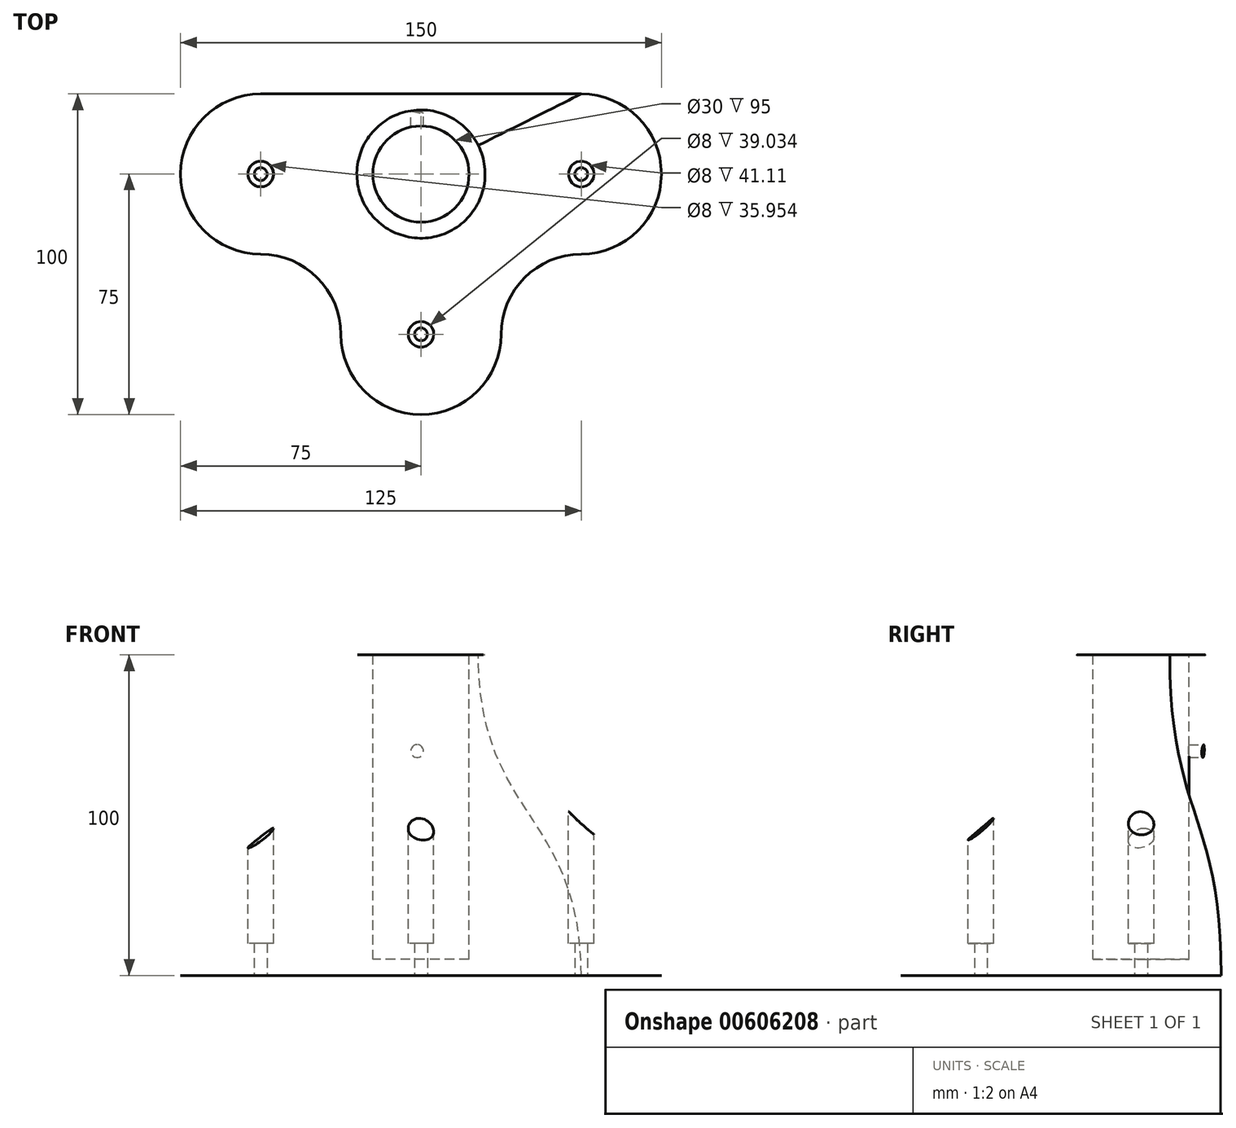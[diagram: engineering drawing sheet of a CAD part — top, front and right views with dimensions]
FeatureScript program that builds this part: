
annotation { "Feature Type Name" : "Feature", "Feature Type Description" : "" }
export const myFeature = defineFeature(function(context is Context, id is Id, definition is map)
    precondition{}
    {
        {
            var Q0;
            Q0=qCreatedBy(makeId("Top.planeOp"),FACE);
            var sketch = newSketch(context, id + "F0", { "sketchPlane" : qUnion([Q0])});
            skLineSegment(sketch, "E0.bottom", {"start": v(-25, 0) * mm, "end": v(-25, 0) * mm});
            skLineSegment(sketch, "E0.top", {"start": v(-25, 50) * mm, "end": v(-125, 50) * mm});
            skLineSegment(sketch, "E0.left", {"start": v(0, 25) * mm, "end": v(0, 25) * mm});
            skLineSegment(sketch, "E0.right", {"start": v(-150, 25) * mm, "end": v(-150, 25) * mm});
            skLineSegment(sketch, "E1", {"start": v(-100, -25) * mm, "end": v(-100, -25) * mm});
            skLineSegment(sketch, "E2", {"start": v(-75, -50) * mm, "end": v(-75, -50) * mm});
            skLineSegment(sketch, "E3", {"start": v(-50, -25) * mm, "end": v(-50, -25) * mm});
            skLineSegment(sketch, "E4.trimOffspring", {"start": v(-125, 0) * mm, "end": v(-125, 0) * mm});
            skPoint(sketch, "E5.visualSharp", {"position": v(0, 50) * mm});
            skArc(sketch, "E5.filletArc", {"start": v(0, 25) * mm, "mid": v(-7.32, 42.68) * mm, "end": v(-25, 50) * mm});
            skPoint(sketch, "E6.visualSharp", {"position": v(0, 0) * mm});
            skArc(sketch, "E6.filletArc", {"start": v(-25, 0) * mm, "mid": v(-7.32, 7.32) * mm, "end": v(0, 25) * mm});
            skPoint(sketch, "E7.visualSharp", {"position": v(-150, 50) * mm});
            skArc(sketch, "E7.filletArc", {"start": v(-125, 50) * mm, "mid": v(-142.68, 42.68) * mm, "end": v(-150, 25) * mm});
            skPoint(sketch, "E8.visualSharp", {"position": v(-150, 0) * mm});
            skArc(sketch, "E8.filletArc", {"start": v(-150, 25) * mm, "mid": v(-142.68, 7.32) * mm, "end": v(-125, 0) * mm});
            skPoint(sketch, "E9.visualSharp", {"position": v(-100, -50) * mm});
            skArc(sketch, "E9.filletArc", {"start": v(-100, -25) * mm, "mid": v(-92.68, -42.68) * mm, "end": v(-75, -50) * mm});
            skPoint(sketch, "E10.visualSharp", {"position": v(-50, -50) * mm});
            skArc(sketch, "E10.filletArc", {"start": v(-75, -50) * mm, "mid": v(-57.32, -42.68) * mm, "end": v(-50, -25) * mm});
            skPoint(sketch, "E11.visualSharp", {"position": v(-50, 0) * mm});
            skArc(sketch, "E11.filletArc", {"start": v(-25, 0) * mm, "mid": v(-42.68, -7.32) * mm, "end": v(-50, -25) * mm});
            skPoint(sketch, "E12.visualSharp", {"position": v(-100, 0) * mm});
            skArc(sketch, "E12.filletArc", {"start": v(-100, -25) * mm, "mid": v(-107.32, -7.32) * mm, "end": v(-125, 0) * mm});
            skSolve(sketch);
        }
        {
            var Q0;
            Q0=qCreatedBy(makeId("Top.planeOp"),FACE);
            cPlane(context, id + "F1", {"entities" : qUnion([Q0]), "cplaneType" : CPlaneType.OFFSET, "offset" : 100 * mm, "width" : 150 * mm, "height" : 150 * mm});
        }
        {
            var Q0;
            Q0=qCreatedBy(id+"F1.planeOp",FACE);
            var sketch = newSketch(context, id + "F2", { "sketchPlane" : qUnion([Q0])});
            skLineSegment(sketch, "E13", {"start": v(-125, 25) * mm, "end": v(-25, 25) * mm, "construction": true});
            skCircle(sketch, "E14", {"center": v(-75, 25) * mm, "radius": 20 * mm});
            skSolve(sketch);
        }
        {
            var Q0;
            Q0=makeQuery(id+"F0.imprint","IMPRINT",FACE,{"disambiguationData":[TD([[makeQuery(id+"F0.imprint","IMPRINT",EDGE,{"derivedFrom":sQuery(id+"F0.wireOp",EDGE,"E0.top")}),1.0]])]});
            var Q1;
            Q1=makeQuery(id+"F2.imprint","IMPRINT",FACE,{"disambiguationData":[TD([[makeQuery(id+"F2.imprint","IMPRINT",EDGE,{"derivedFrom":sQuery(id+"F2.wireOp",EDGE,"E14")}),1.0]])]});
            loft(context, id + "F3", {"startCondition" : LoftEndDerivativeType.NORMAL_TO_PROFILE, "startMagnitude" : 1.5, "endCondition" : LoftEndDerivativeType.NORMAL_TO_PROFILE, "endMagnitude" : 1.5, "sheetProfilesArray" : [{ "sheetProfileEntities" : qUnion([Q0]) }, { "sheetProfileEntities" : qUnion([Q1]) }]});
        }
        {
            var Q0;
            Q0=makeQuery(id+"F3.opLoft","CAP_FACE",FACE,{"disambiguationData":[OSD([makeQuery(id+"F2.imprint","IMPRINT",FACE,{"disambiguationData":[TD([[makeQuery(id+"F2.imprint","IMPRINT",EDGE,{"derivedFrom":sQuery(id+"F2.wireOp",EDGE,"E14")}),1.0]])]})])],"isStart":true});
            var sketch = newSketch(context, id + "F4", { "sketchPlane" : qUnion([Q0])});
            skCircle(sketch, "E15", {"center": v(-75, 25) * mm, "radius": 15 * mm});
            skSolve(sketch);
        }
        {
            var Q0;
            Q0=makeQuery(id+"F4.imprint","IMPRINT",FACE,{"disambiguationData":[TD([[makeQuery(id+"F4.imprint","IMPRINT",EDGE,{"derivedFrom":sQuery(id+"F4.wireOp",EDGE,"E15")}),1.0]])]});
            extrude(context, id + "F5", {"entities" : qUnion([Q0]), "operationType" : NewBodyOperationType.REMOVE, "oppositeDirection" : true, "depth" : 95 * mm, "offsetDistance" : 25 * mm});
        }
        {
            var Q0;
            Q0=makeQuery(id+"F3.opLoft","CAP_FACE",FACE,{"disambiguationData":[OSD([makeQuery(id+"F0.imprint","IMPRINT",FACE,{"disambiguationData":[TD([[makeQuery(id+"F0.imprint","IMPRINT",EDGE,{"derivedFrom":sQuery(id+"F0.wireOp",EDGE,"E0.top")}),1.0]])]})])],"isStart":true});
            var sketch = newSketch(context, id + "F6", { "sketchPlane" : qUnion([Q0])});
            skCircle(sketch, "E16", {"center": v(-25, -25) * mm, "radius": 2 * mm});
            skCircle(sketch, "E17", {"center": v(-75, 25) * mm, "radius": 2 * mm});
            skCircle(sketch, "E18", {"center": v(-125, -25) * mm, "radius": 2 * mm});
            skSolve(sketch);
        }
        {
            var Q0;
            Q0=makeQuery(id+"F6.imprint","IMPRINT",FACE,{"disambiguationData":[TD([[makeQuery(id+"F6.imprint","IMPRINT",EDGE,{"derivedFrom":sQuery(id+"F6.wireOp",EDGE,"E17")}),1.0]])]});
            var Q1;
            Q1=makeQuery(id+"F6.imprint","IMPRINT",FACE,{"disambiguationData":[TD([[makeQuery(id+"F6.imprint","IMPRINT",EDGE,{"derivedFrom":sQuery(id+"F6.wireOp",EDGE,"E16")}),1.0]])]});
            var Q2;
            Q2=makeQuery(id+"F6.imprint","IMPRINT",FACE,{"disambiguationData":[TD([[makeQuery(id+"F6.imprint","IMPRINT",EDGE,{"derivedFrom":sQuery(id+"F6.wireOp",EDGE,"E18")}),1.0]])]});
            extrude(context, id + "F7", {"entities" : qUnion([Q0, Q1, Q2]), "operationType" : NewBodyOperationType.REMOVE, "endBound" : BoundingType.THROUGH_ALL, "oppositeDirection" : true, "depth" : 25 * mm, "offsetDistance" : 25 * mm});
        }
        {
            var Q0;
            Q0=makeQuery(id+"F3.opLoft","CAP_FACE",FACE,{"disambiguationData":[OSD([makeQuery(id+"F2.imprint","IMPRINT",FACE,{"disambiguationData":[TD([[makeQuery(id+"F2.imprint","IMPRINT",EDGE,{"derivedFrom":sQuery(id+"F2.wireOp",EDGE,"E14")}),1.0]])]})])],"isStart":true});
            var sketch = newSketch(context, id + "F8", { "sketchPlane" : qUnion([Q0])});
            skCircle(sketch, "E19", {"center": v(-75, -25) * mm, "radius": 4 * mm});
            skCircle(sketch, "E20", {"center": v(-125, 25) * mm, "radius": 4 * mm});
            skCircle(sketch, "E21", {"center": v(-25, 25) * mm, "radius": 4 * mm});
            skSolve(sketch);
        }
        {
            var Q0;
            Q0=makeQuery(id+"F8.imprint","IMPRINT",FACE,{"disambiguationData":[TD([[makeQuery(id+"F8.imprint","IMPRINT",EDGE,{"derivedFrom":sQuery(id+"F8.wireOp",EDGE,"E20")}),1.0]])]});
            var Q1;
            Q1=makeQuery(id+"F8.imprint","IMPRINT",FACE,{"disambiguationData":[TD([[makeQuery(id+"F8.imprint","IMPRINT",EDGE,{"derivedFrom":sQuery(id+"F8.wireOp",EDGE,"E19")}),1.0]])]});
            var Q2;
            Q2=makeQuery(id+"F8.imprint","IMPRINT",FACE,{"disambiguationData":[TD([[makeQuery(id+"F8.imprint","IMPRINT",EDGE,{"derivedFrom":sQuery(id+"F8.wireOp",EDGE,"E21")}),1.0]])]});
            extrude(context, id + "F9", {"entities" : qUnion([Q0, Q1, Q2]), "operationType" : NewBodyOperationType.REMOVE, "oppositeDirection" : true, "depth" : 90 * mm, "offsetDistance" : 25 * mm});
        }
        {
            var Q0;
            Q0=qCreatedBy(makeId("Front.planeOp"),FACE);
            cPlane(context, id + "F10", {"entities" : qUnion([Q0]), "cplaneType" : CPlaneType.OFFSET, "offset" : 50 * mm, "oppositeDirection" : true, "width" : 150 * mm, "height" : 150 * mm});
        }
        {
            var Q0;
            Q0=qCreatedBy(id+"F10.planeOp",FACE);
            var sketch = newSketch(context, id + "F11", { "sketchPlane" : qUnion([Q0])});
            skLineSegment(sketch, "E22", {"start": v(-76.2, 70) * mm, "end": v(-76.2, 100) * mm, "construction": true});
            skCircle(sketch, "E23", {"center": v(-76.2, 70) * mm, "radius": 2 * mm});
            skSolve(sketch);
        }
        {
            var Q0;
            Q0=makeQuery(id+"F11.imprint","IMPRINT",FACE,{"disambiguationData":[TD([[makeQuery(id+"F11.imprint","IMPRINT",EDGE,{"derivedFrom":sQuery(id+"F11.wireOp",EDGE,"E23")}),1.0]])]});
            extrude(context, id + "F12", {"entities" : qUnion([Q0]), "operationType" : NewBodyOperationType.REMOVE, "depth" : 25 * mm, "offsetDistance" : 25 * mm});
        }
    });
